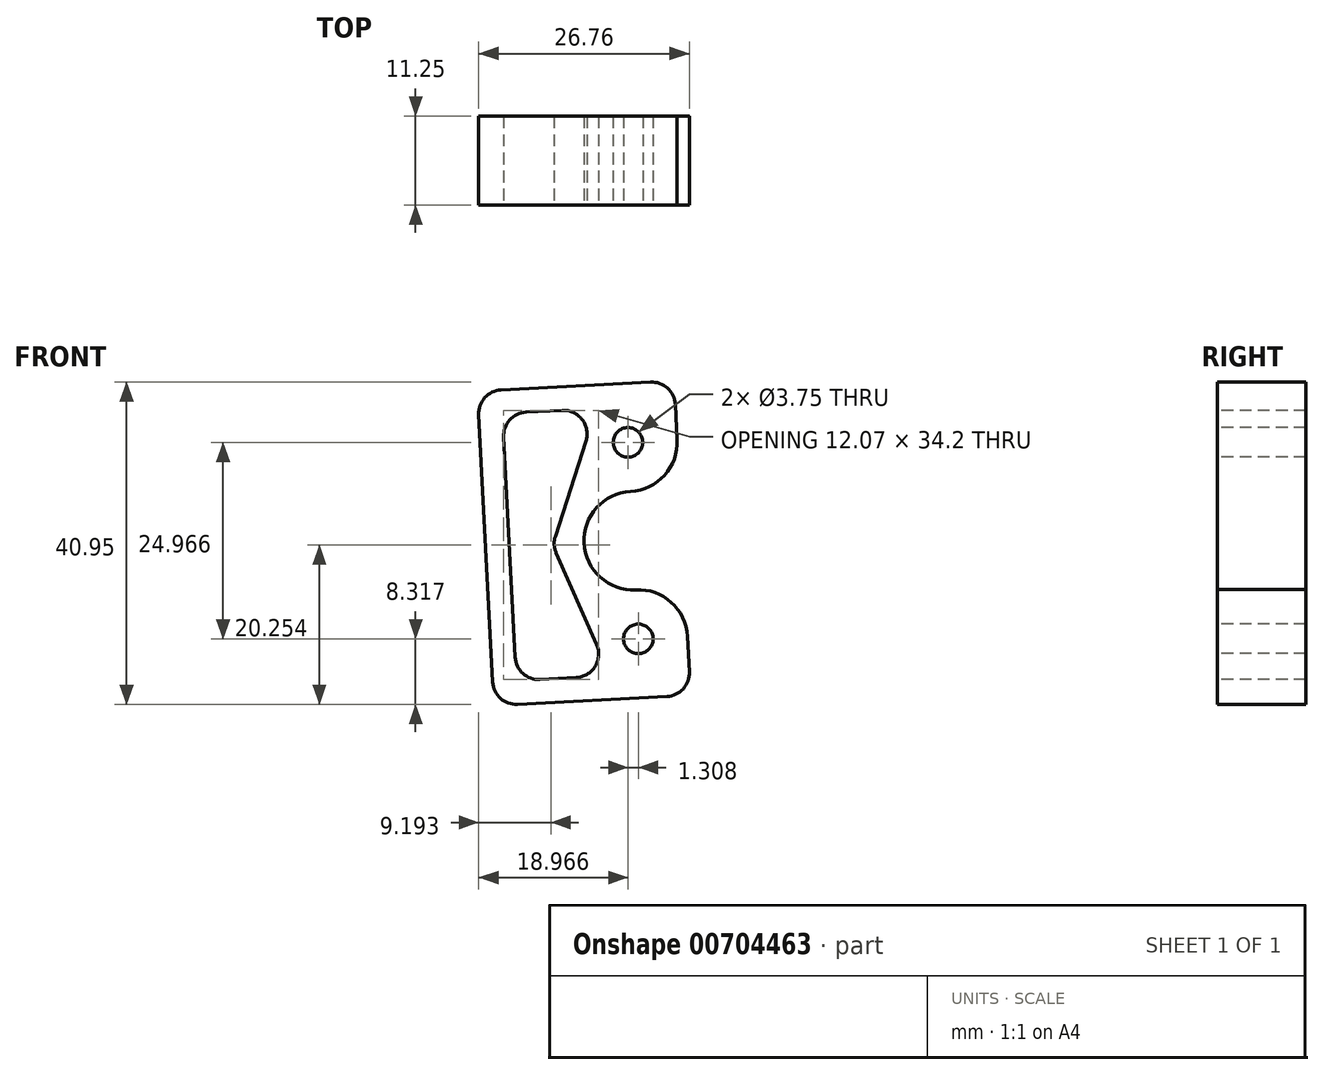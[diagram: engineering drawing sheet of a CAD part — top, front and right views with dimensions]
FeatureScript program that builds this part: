
annotation { "Feature Type Name" : "Feature", "Feature Type Description" : "" }
export const myFeature = defineFeature(function(context is Context, id is Id, definition is map)
    precondition{}
    {
        {
            var Q0;
            Q0=qCreatedBy(makeId("Front.planeOp"),FACE);
            var sketch = newSketch(context, id + "F0", { "sketchPlane" : qUnion([Q0])});
            skCircle(sketch, "E0", {"center": v(0, 0) * mm, "radius": 17.9 * mm, "construction": true});
            skArc(sketch, "E1", {"start": v(0, 6.25) * mm, "mid": v(-6.25, -0.16) * mm, "end": v(0.33, -6.24) * mm, "construction": true});
            skLineSegment(sketch, "E2", {"start": v(0, 17.9) * mm, "end": v(0, -17.9) * mm, "construction": true});
            skLineSegment(sketch, "E3", {"start": v(0, 0) * mm, "end": v(-0.94, 17.88) * mm, "construction": true});
            skLineSegment(sketch, "E4", {"start": v(0, 0) * mm, "end": v(0.94, -17.88) * mm, "construction": true});
            skCircle(sketch, "E5", {"center": v(-0.65, 12.48) * mm, "radius": 1.88 * mm});
            skLineSegment(sketch, "E6", {"start": v(0, 0) * mm, "end": v(17.88, 0.94) * mm, "construction": true});
            skCircle(sketch, "E7.MirrorC", {"center": v(0.65, -12.48) * mm, "radius": 1.88 * mm});
            skLineSegment(sketch, "E8", {"start": v(5.59, 12.8) * mm, "end": v(5.35, 17.3) * mm});
            skLineSegment(sketch, "E9", {"start": v(2.2, 20.14) * mm, "end": v(-16.78, 19.15) * mm});
            skLineSegment(sketch, "E10", {"start": v(-19.61, 16) * mm, "end": v(-18.72, -0.98) * mm});
            skLineSegment(sketch, "E11.MirrorCS", {"start": v(6.9, -12.16) * mm, "end": v(7.13, -16.65) * mm});
            skLineSegment(sketch, "E12.MirrorCS", {"start": v(4.3, -19.8) * mm, "end": v(-14.68, -20.8) * mm});
            skLineSegment(sketch, "E13.MirrorCS", {"start": v(-17.83, -17.96) * mm, "end": v(-18.72, -0.98) * mm});
            skArc(sketch, "E14", {"start": v(-0.33, 6.24) * mm, "mid": v(4, 8.3) * mm, "end": v(5.59, 12.8) * mm});
            skArc(sketch, "E15.MirrorC", {"start": v(-2.82, -17.68) * mm, "mid": v(-2.43, -7.05) * mm, "end": v(6.9, -12.16) * mm});
            skArc(sketch, "E16", {"start": v(0, 6.25) * mm, "mid": v(-6.25, -0.16) * mm, "end": v(0.33, -6.24) * mm});
            skPoint(sketch, "E17.visualSharp", {"position": v(5.2, 20.3) * mm});
            skArc(sketch, "E17.filletArc", {"start": v(5.35, 17.3) * mm, "mid": v(4.36, 19.38) * mm, "end": v(2.2, 20.14) * mm});
            skPoint(sketch, "E18.visualSharp", {"position": v(-19.77, 19) * mm});
            skArc(sketch, "E18.filletArc", {"start": v(-16.78, 19.15) * mm, "mid": v(-18.85, 18.16) * mm, "end": v(-19.61, 16) * mm});
            skPoint(sketch, "E19.visualSharp", {"position": v(-17.68, -20.95) * mm});
            skArc(sketch, "E19.filletArc", {"start": v(-17.83, -17.96) * mm, "mid": v(-16.85, -20.03) * mm, "end": v(-14.68, -20.8) * mm});
            skPoint(sketch, "E20.visualSharp", {"position": v(7.29, -19.65) * mm});
            skArc(sketch, "E20.filletArc", {"start": v(4.3, -19.8) * mm, "mid": v(6.36, -18.81) * mm, "end": v(7.13, -16.65) * mm});
            skSolve(sketch);
        }
        {
            var Q0;
            Q0=makeQuery(id+"F0.imprint","IMPRINT",FACE,{"disambiguationData":[TD([[makeQuery(id+"F0.imprint","IMPRINT",EDGE,{"derivedFrom":sQuery(id+"F0.wireOp",EDGE,"E5")}),-1.0]])]});
            extrude(context, id + "F1", {"entities" : qUnion([Q0]), "oppositeDirection" : true, "depth" : 11.25 * mm, "offsetDistance" : 25 * mm});
        }
        {
            var Q0;
            Q0=makeQuery(id+"F1.opExtrude","CAP_FACE",FACE,{"disambiguationData":[OSD([sQuery(id+"F0.wireOp",EDGE,"E5"),sQuery(id+"F0.wireOp",EDGE,"E7.MirrorC"),sQuery(id+"F0.wireOp",EDGE,"E8"),sQuery(id+"F0.wireOp",EDGE,"E9"),sQuery(id+"F0.wireOp",EDGE,"E10"),sQuery(id+"F0.wireOp",EDGE,"E11.MirrorCS"),sQuery(id+"F0.wireOp",EDGE,"E12.MirrorCS"),sQuery(id+"F0.wireOp",EDGE,"E13.MirrorCS"),sQuery(id+"F0.wireOp",EDGE,"E14"),sQuery(id+"F0.wireOp",EDGE,"E15.MirrorC"),sQuery(id+"F0.wireOp",EDGE,"E16"),sQuery(id+"F0.wireOp",EDGE,"E17.filletArc"),sQuery(id+"F0.wireOp",EDGE,"E18.filletArc"),sQuery(id+"F0.wireOp",EDGE,"E19.filletArc"),sQuery(id+"F0.wireOp",EDGE,"E20.filletArc")])],"isStart":true});
            var sketch = newSketch(context, id + "F2", { "sketchPlane" : qUnion([Q0])});
            skLineSegment(sketch, "E21.1", {"start": v(-11.84, -17.64) * mm, "end": v(-7.23, -17.4) * mm});
            skLineSegment(sketch, "E21.3", {"start": v(-16.46, 13.16) * mm, "end": v(-15, -14.8) * mm});
            skLineSegment(sketch, "E21.7", {"start": v(-9, 16.55) * mm, "end": v(-13.62, 16.3) * mm});
            skLineSegment(sketch, "E22", {"start": v(0, 0) * mm, "end": v(-18.72, -0.98) * mm, "construction": true});
            skLineSegment(sketch, "E23", {"start": v(-6, 12.64) * mm, "end": v(-9.89, 0.55) * mm});
            skLineSegment(sketch, "E24.MirrorCS", {"start": v(-4.64, -13.2) * mm, "end": v(-9.77, -1.58) * mm});
            skPoint(sketch, "E25.visualSharp", {"position": v(-4.66, 16.78) * mm});
            skArc(sketch, "E25.filletArc", {"start": v(-6, 12.64) * mm, "mid": v(-6.47, 15.38) * mm, "end": v(-9, 16.55) * mm});
            skPoint(sketch, "E26.visualSharp", {"position": v(-16.62, 16.15) * mm});
            skArc(sketch, "E26.filletArc", {"start": v(-13.62, 16.3) * mm, "mid": v(-15.7, 15.32) * mm, "end": v(-16.46, 13.16) * mm});
            skPoint(sketch, "E27.visualSharp", {"position": v(-14.84, -17.8) * mm});
            skArc(sketch, "E27.filletArc", {"start": v(-15, -14.8) * mm, "mid": v(-14, -16.88) * mm, "end": v(-11.84, -17.64) * mm});
            skPoint(sketch, "E28.visualSharp", {"position": v(-2.88, -17.17) * mm});
            skArc(sketch, "E28.filletArc", {"start": v(-7.23, -17.4) * mm, "mid": v(-4.83, -15.98) * mm, "end": v(-4.64, -13.2) * mm});
            skPoint(sketch, "E29.visualSharp", {"position": v(-10.24, -0.54) * mm});
            skArc(sketch, "E29.filletArc", {"start": v(-9.89, 0.55) * mm, "mid": v(-10.03, -0.53) * mm, "end": v(-9.77, -1.58) * mm});
            skSolve(sketch);
        }
        {
            var Q0;
            Q0=makeQuery(id+"F2.imprint","IMPRINT",FACE,{"disambiguationData":[TD([[makeQuery(id+"F2.imprint","IMPRINT",EDGE,{"derivedFrom":sQuery(id+"F2.wireOp",EDGE,"E21.1")}),1.0]])]});
            extrude(context, id + "F3", {"entities" : qUnion([Q0]), "operationType" : NewBodyOperationType.REMOVE, "oppositeDirection" : true, "depth" : 25 * mm, "offsetDistance" : 25 * mm});
        }
    });
